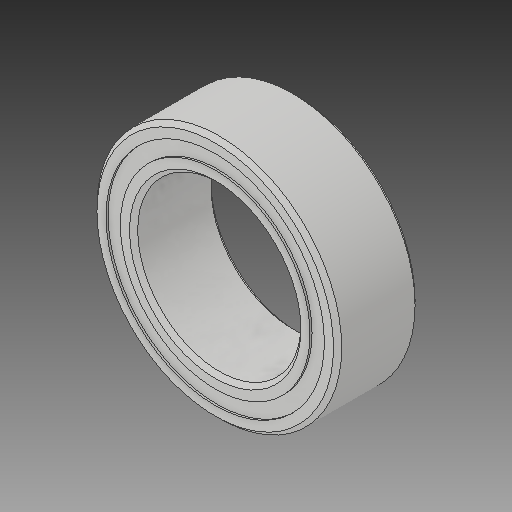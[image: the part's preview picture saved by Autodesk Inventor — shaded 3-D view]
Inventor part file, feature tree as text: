
AUTODESK INVENTOR PART (.ipt)
format: ipt  version: 2017 (Build 210142000, 142)  size: 603,136 bytes
history: native  units: in
note: dims shown in document units (in); Inventor stores cm internally (conversion verified against a paired STEP export)
features: other x11, revolve x5
ambient origin geometry x8: Origin, YZ Plane, XZ Plane, XY Plane, X Axis, Y Axis, Z Axis, Center Point
bodies: Solid1 (feature_tree), Solid2 (feature_tree), Solid3 (feature_tree), Solid4 (feature_tree), Solid5 (feature_tree), Solid6 (feature_tree), Solid7 (feature_tree), Solid8 (feature_tree), Solid9 (feature_tree), Solid10 (feature_tree), Solid11 (feature_tree), Solid12 (feature_tree), Solid13 (feature_tree), Solid14 (feature_tree), Solid15 (feature_tree), Solid16 (feature_tree)
feature tree (16):
  revolve  "Revolve1"  [1 undecoded]
  revolve  "Revolve3"  [1 undecoded]
  revolve  "Revolve4"  [1 undecoded]
  other  "CirPattern1[1]"
  other  "CirPattern1[2]"
  other  "CirPattern1[3]"
  other  "CirPattern1[4]"
  other  "CirPattern1[5]"
  other  "CirPattern1[6]"
  other  "CirPattern1[7]"
  other  "CirPattern1[8]"
  other  "CirPattern1[9]"
  other  "CirPattern1[10]"
  other  "CirPattern1[11]"
  revolve  "Revolve5[1]"  [1 undecoded]
  revolve  "Revolve5[2]"  [1 undecoded]
note: 5 required parameter values undecoded (feature->parameter linkage not recoverable at this tier; creation-order binding heuristic only, values carry confidence <= 0.55)
